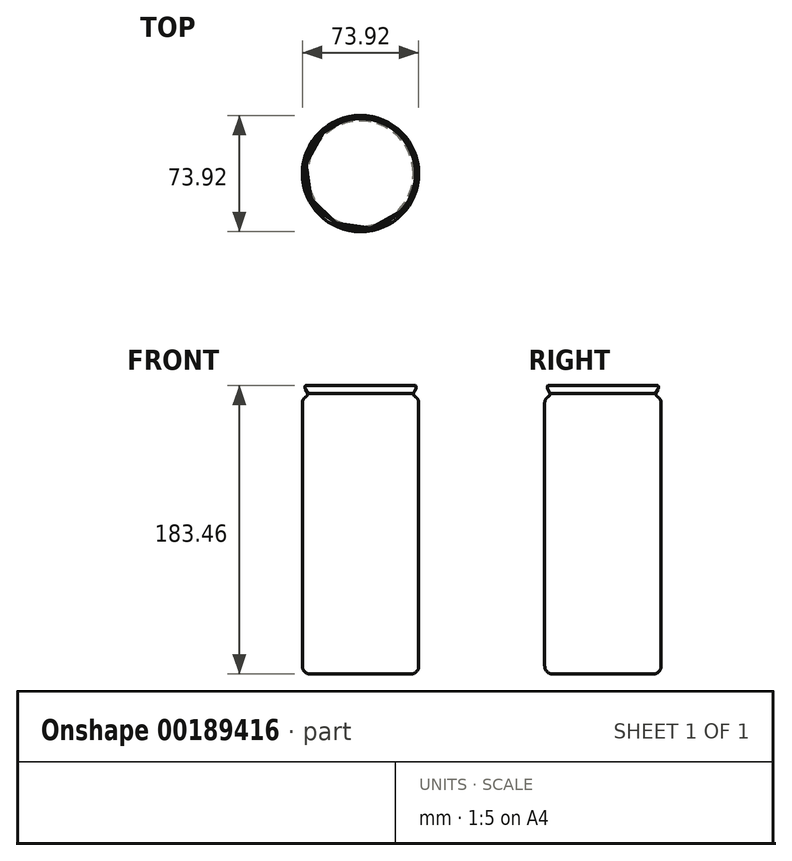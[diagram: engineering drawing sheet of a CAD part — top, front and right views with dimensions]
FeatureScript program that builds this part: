
annotation { "Feature Type Name" : "Feature", "Feature Type Description" : "" }
export const myFeature = defineFeature(function(context is Context, id is Id, definition is map)
    precondition{}
    {
        {
            var Q0;
            Q0=qCreatedBy(makeId("Top.planeOp"),FACE);
            var sketch = newSketch(context, id + "F0", { "sketchPlane" : qUnion([Q0])});
            skCircle(sketch, "E0", {"center": v(0, 0) * mm, "radius": 36.96 * mm});
            skSolve(sketch);
        }
        {
            var Q0;
            Q0 = qSketchRegion(id + "F0", true);
            extrude(context, id + "F1", {"entities" : qUnion([Q0]), "depth" : 172.44 * mm});
        }
        {
            var Q0;
            Q0=qCreatedBy(makeId("Front.planeOp"),FACE);
            var sketch = newSketch(context, id + "F2", { "sketchPlane" : qUnion([Q0])});
            skArc(sketch, "E1", {"start": v(36.96, 172.44) * mm, "mid": v(36.42, 174.5) * mm, "end": v(34.94, 176.03) * mm});
            skArc(sketch, "E2", {"start": v(33.5, 178.18) * mm, "mid": v(33.98, 176.94) * mm, "end": v(34.94, 176.03) * mm});
            skLineSegment(sketch, "E3", {"start": v(33.5, 178.18) * mm, "end": v(34.94, 180.92) * mm});
            skArc(sketch, "E4", {"start": v(34.94, 180.92) * mm, "mid": v(35.25, 182.2) * mm, "end": v(34.94, 183.46) * mm});
            skPoint(sketch, "E5", {"position": v(35.25, 182.2) * mm});
            skPoint(sketch, "E6", {"position": v(33.98, 176.94) * mm});
            skLineSegment(sketch, "E7", {"start": v(34.94, 183.46) * mm, "end": v(0, 183.46) * mm});
            skLineSegment(sketch, "E8", {"start": v(0, 183.46) * mm, "end": v(0, 172.44) * mm});
            skLineSegment(sketch, "E9", {"start": v(0, 172.44) * mm, "end": v(36.96, 172.44) * mm});
            skSolve(sketch);
        }
        {
            var Q0;
            Q0 = qSketchRegion(id + "F2", true);
            var Q1;
            Q1=sQuery(id+"F2.wireOp",EDGE,"E8");
            revolve(context, id + "F3", {"operationType" : NewBodyOperationType.ADD, "entities" : qUnion([Q0]), "axis" : qUnion([Q1]), "revolveType" : RevolveType.FULL});
        }
        {
            var Q0;
            Q0=makeQuery(id+"F1.opExtrude","CAP_EDGE",EDGE,{"disambiguationData":[OSD([sQuery(id+"F0.wireOp",EDGE,"E0")])],"isStart":true});
            fillet(context, id + "F4", {"entities" : qUnion([Q0]), "radius" : 5.08 * mm, "tangentPropagation" : true, "allowEdgeOverflow" : false});
        }
    });
